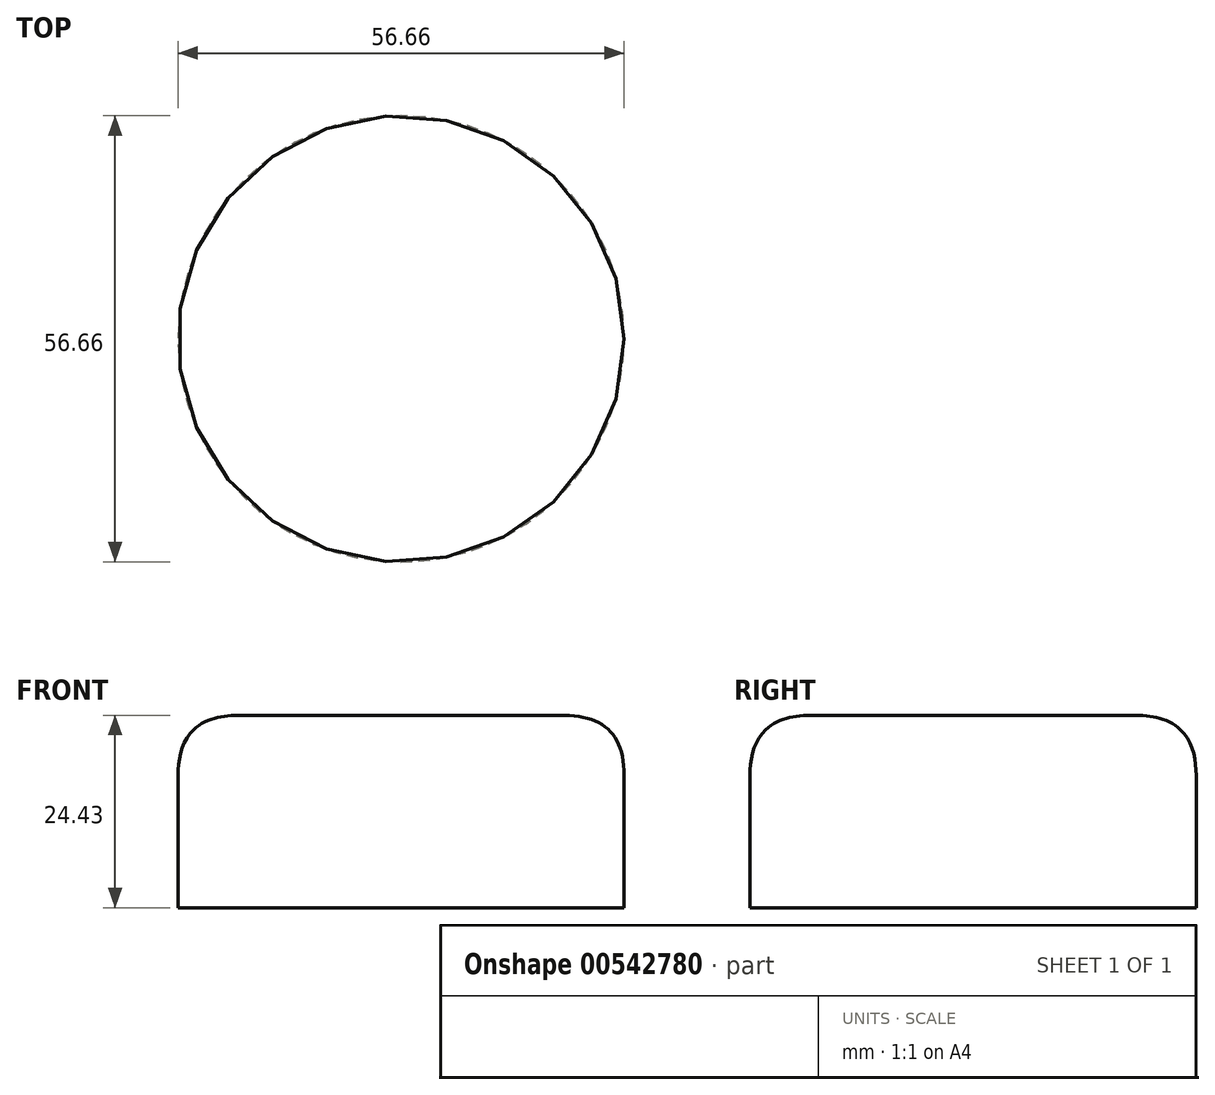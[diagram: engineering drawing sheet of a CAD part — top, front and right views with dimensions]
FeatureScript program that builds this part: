
annotation { "Feature Type Name" : "Feature", "Feature Type Description" : "" }
export const myFeature = defineFeature(function(context is Context, id is Id, definition is map)
    precondition{}
    {
        {
            var Q0;
            Q0=qCreatedBy(makeId("Top.planeOp"),FACE);
            var sketch = newSketch(context, id + "F0", { "sketchPlane" : qUnion([Q0])});
            skCircle(sketch, "E0", {"center": v(0, 0) * mm, "radius": 28.33 * mm});
            skSolve(sketch);
        }
        {
            var Q0;
            Q0=makeQuery(id+"F0.imprint","IMPRINT",FACE,{"disambiguationData":[TD([[makeQuery(id+"F0.imprint","IMPRINT",EDGE,{"derivedFrom":sQuery(id+"F0.wireOp",EDGE,"E0")}),1.0]])]});
            extrude(context, id + "F1", {"entities" : qUnion([Q0]), "depth" : 24.43 * mm, "offsetDistance" : 25.4 * mm, "hasDraft" : true, "draftAngle" : 0 * degree});
        }
        {
            var Q0;
            Q0=makeQuery(id+"F1.opExtrude","CAP_EDGE",EDGE,{"disambiguationData":[OSD([sQuery(id+"F0.wireOp",EDGE,"E0")])],"isStart":false});
            fillet(context, id + "F2", {"entities" : qUnion([Q0]), "radius" : 7.62 * mm, "tangentPropagation" : true, "rho" : 0.5, "crossSection" : FilletCrossSection.CONIC, "allowEdgeOverflow" : false});
        }
    });
